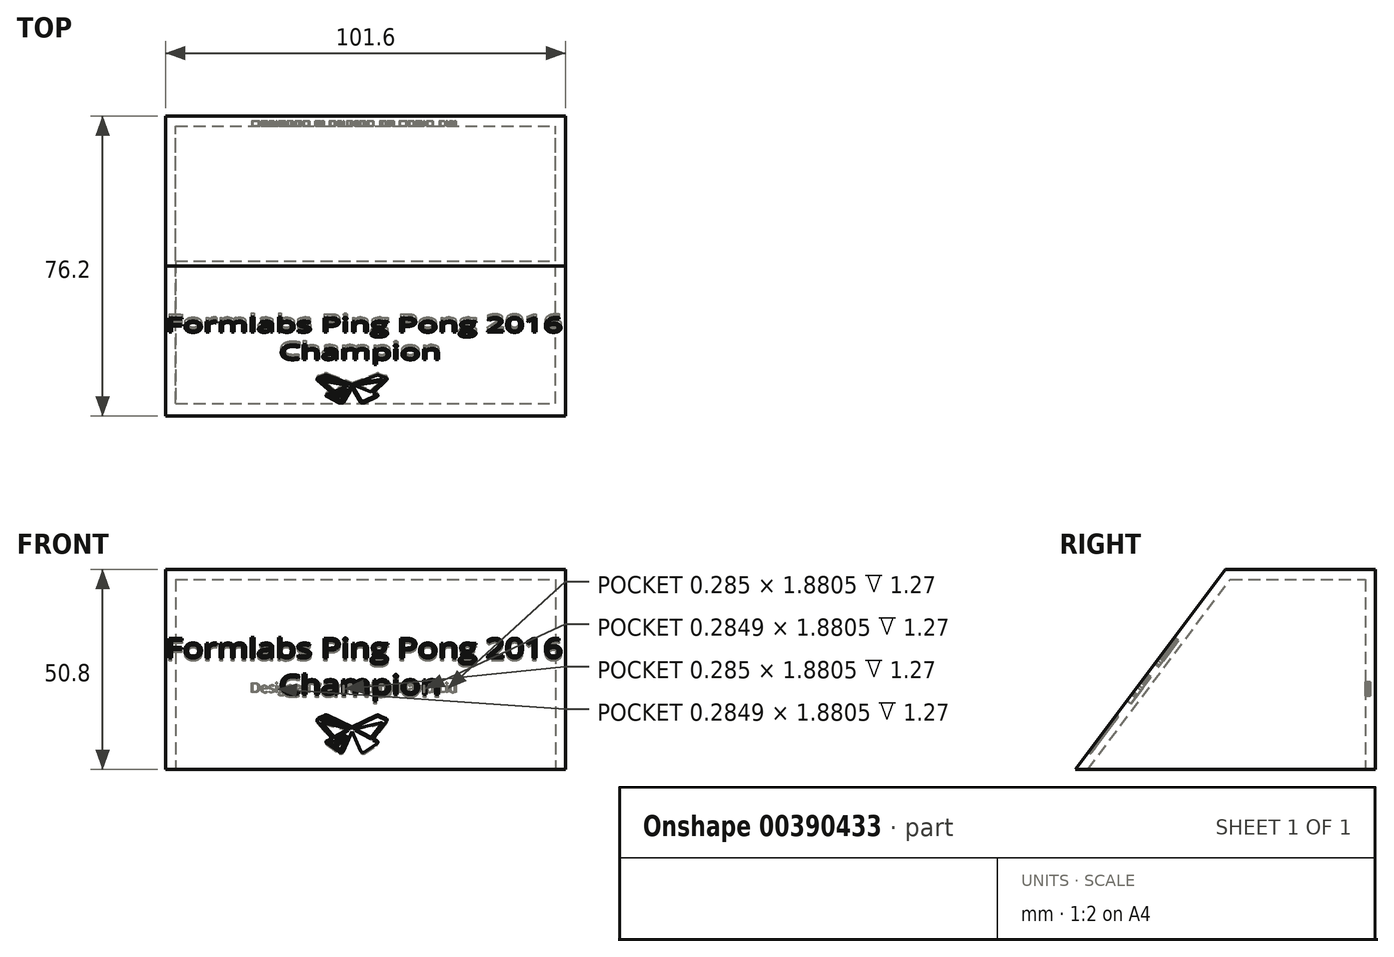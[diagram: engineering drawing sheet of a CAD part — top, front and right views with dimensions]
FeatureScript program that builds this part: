
annotation { "Feature Type Name" : "Feature", "Feature Type Description" : "" }
export const myFeature = defineFeature(function(context is Context, id is Id, definition is map)
    precondition{}
    {
        {
            var Q0;
            Q0=qCreatedBy(makeId("Top.planeOp"),FACE);
            var sketch = newSketch(context, id + "F0", { "sketchPlane" : qUnion([Q0])});
            skLineSegment(sketch, "E0.bottom", {"start": v(-33.87, 0) * mm, "end": v(67.73, 0) * mm});
            skLineSegment(sketch, "E0.top", {"start": v(-33.87, 76.2) * mm, "end": v(67.73, 76.2) * mm});
            skLineSegment(sketch, "E0.left", {"start": v(-33.87, 0) * mm, "end": v(-33.87, 76.2) * mm});
            skLineSegment(sketch, "E0.right", {"start": v(67.73, 0) * mm, "end": v(67.73, 76.2) * mm});
            skSolve(sketch);
        }
        {
            var Q0;
            Q0=makeQuery(id+"F0.imprint","IMPRINT",FACE,{"disambiguationData":[TD([[makeQuery(id+"F0.imprint","IMPRINT",EDGE,{"derivedFrom":sQuery(id+"F0.wireOp",EDGE,"E0.bottom")}),1.0]])]});
            extrude(context, id + "F1", {"entities" : qUnion([Q0]), "depth" : 50.8 * mm});
        }
        {
            var Q0;
            Q0=makeQuery(id+"F1.opExtrude","SWEPT_FACE",FACE,{"disambiguationData":[OSD([sQuery(id+"F0.wireOp",EDGE,"E0.right")])]});
            var sketch = newSketch(context, id + "F2", { "sketchPlane" : qUnion([Q0])});
            skLineSegment(sketch, "E1", {"start": v(0, 0) * mm, "end": v(38.1, 50.8) * mm});
            skLineSegment(sketch, "E2", {"start": v(38.1, 50.8) * mm, "end": v(0, 50.8) * mm});
            skLineSegment(sketch, "E3", {"start": v(0, 50.8) * mm, "end": v(0, 0) * mm});
            skSolve(sketch);
        }
        {
            var Q0;
            Q0=makeQuery(id+"F2.imprint","IMPRINT",FACE,{"disambiguationData":[TD([[makeQuery(id+"F2.imprint","IMPRINT",EDGE,{"derivedFrom":sQuery(id+"F2.wireOp",EDGE,"E1")}),1.0]])]});
            extrude(context, id + "F3", {"entities" : qUnion([Q0]), "operationType" : NewBodyOperationType.REMOVE, "endBound" : BoundingType.THROUGH_ALL, "oppositeDirection" : true, "depth" : 25.4 * mm});
        }
        {
            var Q0;
            Q0=makeQuery(id+"F1.opExtrude","CAP_FACE",FACE,{"disambiguationData":[OSD([sQuery(id+"F0.wireOp",EDGE,"E0.bottom"),sQuery(id+"F0.wireOp",EDGE,"E0.top"),sQuery(id+"F0.wireOp",EDGE,"E0.left"),sQuery(id+"F0.wireOp",EDGE,"E0.right")])],"isStart":true});
            shell(context, id + "F4", {"entities" : qUnion([Q0]), "thickness" : 2.54 * mm});
        }
        {
            var Q0;
            Q0=makeQuery(id+"F3.boolean.opBoolean","COPY",FACE,{"derivedFrom":makeQuery(id+"F3.opExtrude","SWEPT_FACE",FACE,{"disambiguationData":[OSD([sQuery(id+"F2.wireOp",EDGE,"E1")])]})});
            var sketch = newSketch(context, id + "F5", { "sketchPlane" : qUnion([Q0])});
            skText(sketch, "E4", { "text": "Formlabs Ping Pong 2016\n             Champion", "fontName": "OpenSans-Regular.ttf"});
            const initialGuessF5  = {"E4": [-0.03388, 0.03549, 1, 0, 0.00615]};
            skSetInitialGuess(sketch, initialGuessF5);
            skSolve(sketch);
        }
        {
            var Q0;
            Q0 = qSketchRegion(id + "F5", true);
            extrude(context, id + "F6", {"entities" : qUnion([Q0]), "operationType" : NewBodyOperationType.REMOVE, "oppositeDirection" : true, "depth" : 1.27 * mm});
        }
        {
            var Q0;
            {var subQ1=sQuery(id+"F0.wireOp",EDGE,"E0.left");Q0=makeQuery(id+"F6.boolean.opBoolean","SPLIT",FACE,{"disambiguationData":[TD([makeQuery(id+"F1.opExtrude","SWEPT_FACE",FACE,{"disambiguationData":[OSD([subQ1])]})])],"derivedFrom":makeQuery(id+"F3.boolean.opBoolean","COPY",FACE,{"derivedFrom":makeQuery(id+"F3.opExtrude","SWEPT_FACE",FACE,{"disambiguationData":[OSD([sQuery(id+"F2.wireOp",EDGE,"E1")])]})})});}
            var sketch = newSketch(context, id + "F7", { "sketchPlane" : qUnion([Q0])});
            skLineSegment(sketch, "E5", {"start": v(7.36, 17.12) * mm, "end": v(13.48, 13.43) * mm});
            skLineSegment(sketch, "E6", {"start": v(13.48, 13.43) * mm, "end": v(19.63, 17.12) * mm});
            skLineSegment(sketch, "E7", {"start": v(21.3, 14.9) * mm, "end": v(14.26, 12.82) * mm});
            skLineSegment(sketch, "E8", {"start": v(14.26, 12.82) * mm, "end": v(18.27, 10.15) * mm});
            skLineSegment(sketch, "E9", {"start": v(18.27, 10.15) * mm, "end": v(21.3, 14.9) * mm});
            skLineSegment(sketch, "E10", {"start": v(22.26, 15.24) * mm, "end": v(18.81, 9.77) * mm});
            skLineSegment(sketch, "E11", {"start": v(18.81, 9.77) * mm, "end": v(19.74, 9.2) * mm});
            skLineSegment(sketch, "E12", {"start": v(12.62, 12.84) * mm, "end": v(8.98, 10.35) * mm});
            skLineSegment(sketch, "E13", {"start": v(8.98, 10.35) * mm, "end": v(5.87, 14.9) * mm});
            skLineSegment(sketch, "E14", {"start": v(5.87, 14.9) * mm, "end": v(12.62, 12.84) * mm});
            skLineSegment(sketch, "E15", {"start": v(11.48, 11.05) * mm, "end": v(9.95, 8.92) * mm});
            skLineSegment(sketch, "E16", {"start": v(9.95, 8.92) * mm, "end": v(9.46, 9.61) * mm});
            skLineSegment(sketch, "E17", {"start": v(9.46, 9.61) * mm, "end": v(11.48, 11.05) * mm});
            skLineSegment(sketch, "E18", {"start": v(12.25, 10.8) * mm, "end": v(10.73, 6.26) * mm});
            skLineSegment(sketch, "E19", {"start": v(10.73, 6.26) * mm, "end": v(7.92, 8.58) * mm});
            skLineSegment(sketch, "E20", {"start": v(7.92, 8.58) * mm, "end": v(8.75, 9.23) * mm});
            skLineSegment(sketch, "E21", {"start": v(7.06, 16.43) * mm, "end": v(10.55, 14.3) * mm});
            skLineSegment(sketch, "E22", {"start": v(10.55, 14.3) * mm, "end": v(5.8, 15.73) * mm});
            skLineSegment(sketch, "E23", {"start": v(5.8, 15.73) * mm, "end": v(7.06, 16.43) * mm});
            skLineSegment(sketch, "E24", {"start": v(13.5, 12.14) * mm, "end": v(15.58, 5.93) * mm});
            skLineSegment(sketch, "E25", {"start": v(13.5, 12.14) * mm, "end": v(11.34, 5.9) * mm});
            skLineSegment(sketch, "E26", {"start": v(7.14, 8.19) * mm, "end": v(10.22, 5.56) * mm});
            skLineSegment(sketch, "E27", {"start": v(8.25, 9.94) * mm, "end": v(7.08, 9.13) * mm});
            skLineSegment(sketch, "E28", {"start": v(5.04, 16.35) * mm, "end": v(6.52, 17.23) * mm});
            skLineSegment(sketch, "E29", {"start": v(20.34, 17.22) * mm, "end": v(22.03, 16.28) * mm});
            skLineSegment(sketch, "E30", {"start": v(16.53, 5.46) * mm, "end": v(19.73, 8.08) * mm});
            skLineSegment(sketch, "E31", {"start": v(12.25, 10.8) * mm, "end": v(10.27, 8.05) * mm});
            skArc(sketch, "E32", {"start": v(5.04, 16.35) * mm, "mid": v(4.6, 15.76) * mm, "end": v(4.7, 15.02) * mm});
            skArc(sketch, "E33", {"start": v(6.52, 17.23) * mm, "mid": v(6.96, 17.32) * mm, "end": v(7.36, 17.12) * mm});
            skArc(sketch, "E34", {"start": v(7.08, 9.13) * mm, "mid": v(6.85, 8.65) * mm, "end": v(7.14, 8.19) * mm});
            skArc(sketch, "E35", {"start": v(11.34, 5.9) * mm, "mid": v(10.87, 5.44) * mm, "end": v(10.22, 5.56) * mm});
            skArc(sketch, "E36", {"start": v(15.58, 5.93) * mm, "mid": v(15.96, 5.5) * mm, "end": v(16.53, 5.46) * mm});
            skArc(sketch, "E37", {"start": v(19.74, 9.2) * mm, "mid": v(20.04, 8.64) * mm, "end": v(19.73, 8.08) * mm});
            skArc(sketch, "E38", {"start": v(22.03, 16.28) * mm, "mid": v(22.38, 15.81) * mm, "end": v(22.26, 15.24) * mm});
            skArc(sketch, "E39", {"start": v(20.34, 17.22) * mm, "mid": v(19.97, 17.29) * mm, "end": v(19.63, 17.12) * mm});
            skArc(sketch, "E40", {"start": v(9.43, 8.25) * mm, "mid": v(9.8, 8) * mm, "end": v(10.27, 8.05) * mm});
            skLineSegment(sketch, "E41", {"start": v(4.7, 15.02) * mm, "end": v(8.25, 9.94) * mm});
            skLineSegment(sketch, "E42", {"start": v(8.75, 9.23) * mm, "end": v(9.43, 8.25) * mm});
            skSolve(sketch);
        }
        {
            var Q0;
            Q0=makeQuery(id+"F7.imprint","IMPRINT",FACE,{"disambiguationData":[TD([[makeQuery(id+"F7.imprint","IMPRINT",EDGE,{"derivedFrom":sQuery(id+"F7.wireOp",EDGE,"E5")}),-1.0]])]});
            extrude(context, id + "F8", {"entities" : qUnion([Q0]), "operationType" : NewBodyOperationType.REMOVE, "oppositeDirection" : true, "depth" : 0.64 * mm});
        }
        {
            var Q0;
            Q0=makeQuery(id+"F4.opShell","OFFSET_FACE",FACE,{"disambiguationData":[OSD([sQuery(id+"F0.wireOp",EDGE,"E0.top")])]});
            var sketch = newSketch(context, id + "F9", { "sketchPlane" : qUnion([Q0])});
            skText(sketch, "E43", { "text": "Designed & Printed by David Liu", "fontName": "OpenSans-Regular.ttf"});
            const initialGuessF9  = {"E43": [-0.01236, 0.01952, 1, 0, 0.00253]};
            skSetInitialGuess(sketch, initialGuessF9);
            skSolve(sketch);
        }
        {
            var Q0;
            Q0 = qSketchRegion(id + "F9", true);
            extrude(context, id + "F10", {"entities" : qUnion([Q0]), "operationType" : NewBodyOperationType.REMOVE, "oppositeDirection" : true, "depth" : 1.27 * mm});
        }
    });
